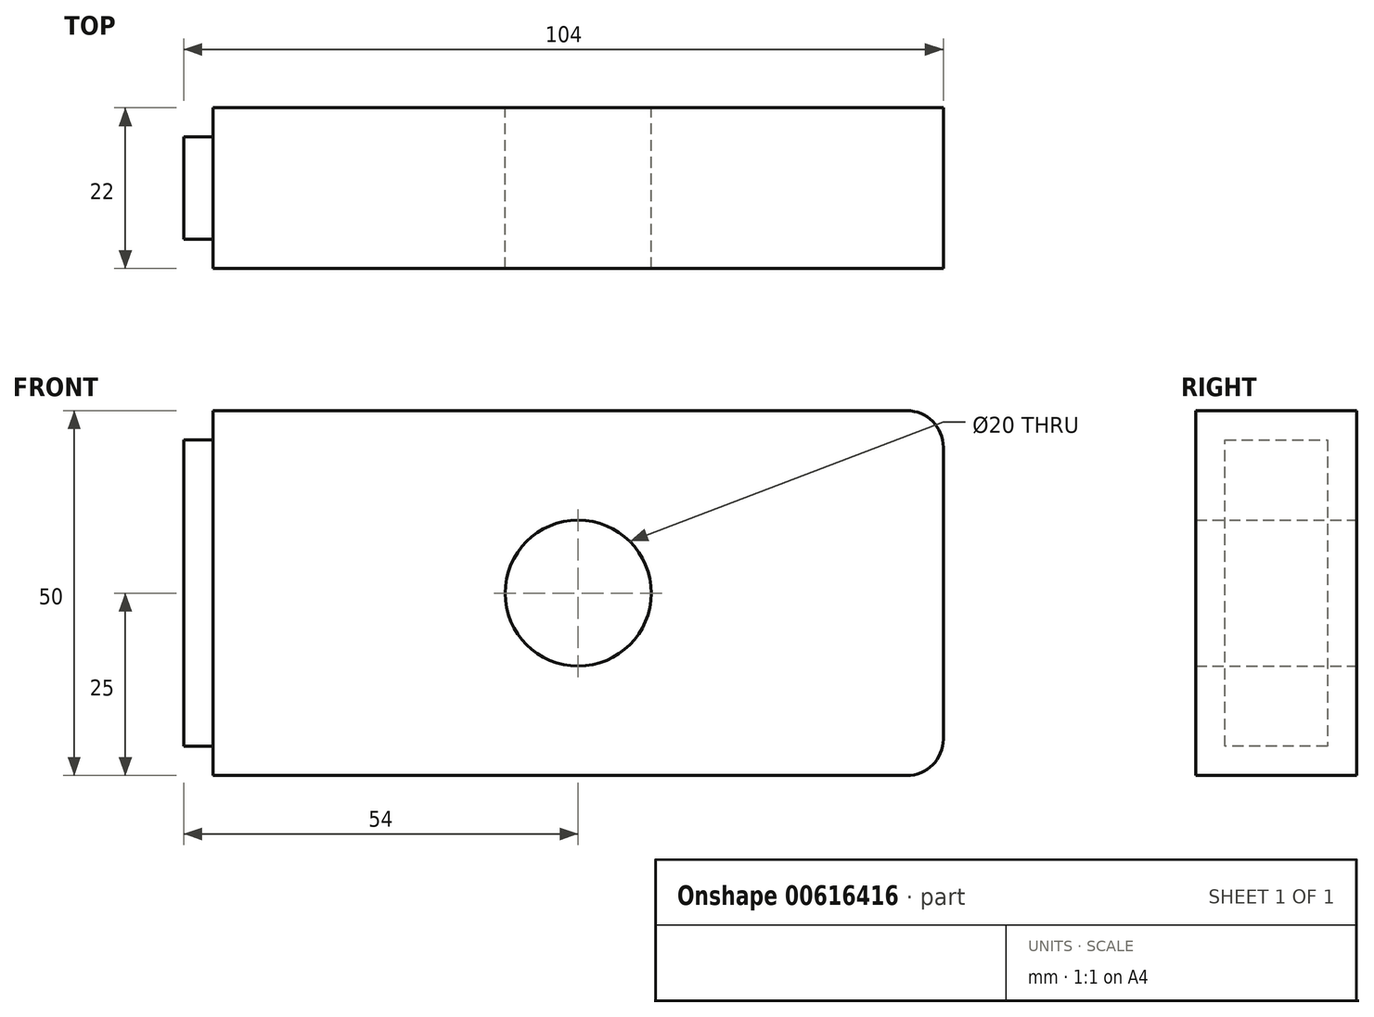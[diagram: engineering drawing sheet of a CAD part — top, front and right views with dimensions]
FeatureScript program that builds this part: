
annotation { "Feature Type Name" : "Feature", "Feature Type Description" : "" }
export const myFeature = defineFeature(function(context is Context, id is Id, definition is map)
    precondition{}
    {
        {
            var Q0;
            Q0=qCreatedBy(makeId("Front.planeOp"),FACE);
            var sketch = newSketch(context, id + "F0", { "sketchPlane" : qUnion([Q0])});
            skLineSegment(sketch, "E0.bottom", {"start": v(-50, 25) * mm, "end": v(45, 25) * mm});
            skLineSegment(sketch, "E0.top", {"start": v(-50, -25) * mm, "end": v(45, -25) * mm});
            skLineSegment(sketch, "E0.left", {"start": v(-50, 25) * mm, "end": v(-50, -25) * mm});
            skLineSegment(sketch, "E0.right", {"start": v(50, 20) * mm, "end": v(50, -20) * mm});
            skCircle(sketch, "E1", {"center": v(0, 0) * mm, "radius": 10 * mm});
            skLineSegment(sketch, "E2", {"start": v(-50, 0) * mm, "end": v(50, 0) * mm, "construction": true});
            skPoint(sketch, "E3.visualSharp", {"position": v(50, 25) * mm});
            skArc(sketch, "E3.filletArc", {"start": v(50, 20) * mm, "mid": v(48.54, 23.54) * mm, "end": v(45, 25) * mm});
            skPoint(sketch, "E4.visualSharp", {"position": v(50, -25) * mm});
            skArc(sketch, "E4.filletArc", {"start": v(45, -25) * mm, "mid": v(48.54, -23.54) * mm, "end": v(50, -20) * mm});
            skSolve(sketch);
        }
        {
            var Q0;
            Q0 = qSketchRegion(id + "F0", true);
            extrude(context, id + "F1", {"entities" : qUnion([Q0]), "depth" : 20 * mm, "offsetDistance" : 25 * mm});
        }
        {
            var Q0;
            Q0 = qSketchRegion(id + "F0", true);
            var Q1;
            Q1=makeQuery(id+"F1.opExtrude","CAP_FACE",FACE,{"disambiguationData":[OSD([sQuery(id+"F0.wireOp",EDGE,"E0.bottom"),sQuery(id+"F0.wireOp",EDGE,"E0.top"),sQuery(id+"F0.wireOp",EDGE,"E0.left"),sQuery(id+"F0.wireOp",EDGE,"E0.right"),sQuery(id+"F0.wireOp",EDGE,"E1")])],"isStart":false});
            extrude(context, id + "F2", {"entities" : qUnion([Q0, Q1]), "operationType" : NewBodyOperationType.ADD, "depth" : 2 * mm, "offsetDistance" : 25 * mm});
        }
        {
            var Q0;
            {var subQ0=sQuery(id+"F0.wireOp",EDGE,"E0.left");Q0=makeQuery(id+"F2.boolean.opBoolean","MERGE",FACE,{"derivedFrom":[makeQuery(id+"F1.opExtrude","SWEPT_FACE",FACE,{"disambiguationData":[OSD([subQ0])]}),makeQuery(id+"F2.opExtrude","SWEPT_FACE",FACE,{"disambiguationData":[OSD([subQ0]),TDD([makeQuery(id+"F1.opExtrude","CAP_EDGE",EDGE,{"disambiguationData":[OSD([subQ0])],"isStart":false})])]})]});}
            var sketch = newSketch(context, id + "F3", { "sketchPlane" : qUnion([Q0])});
            skLineSegment(sketch, "E5.0", {"start": v(18, 21) * mm, "end": v(4, 21) * mm});
            skLineSegment(sketch, "E5.1", {"start": v(18, -21) * mm, "end": v(18, 21) * mm});
            skLineSegment(sketch, "E5.2", {"start": v(4, -21) * mm, "end": v(18, -21) * mm});
            skLineSegment(sketch, "E5.3", {"start": v(4, 21) * mm, "end": v(4, -21) * mm});
            skSolve(sketch);
        }
        {
            var Q0;
            Q0=makeQuery(id+"F3.imprint","IMPRINT",FACE,{"disambiguationData":[TD([[makeQuery(id+"F3.imprint","IMPRINT",EDGE,{"derivedFrom":sQuery(id+"F3.wireOp",EDGE,"E5.0")}),1.0]])]});
            extrude(context, id + "F4", {"entities" : qUnion([Q0]), "operationType" : NewBodyOperationType.ADD, "depth" : 4 * mm, "offsetDistance" : 25 * mm});
        }
        {
            var Q0;
            {var subQ0=sQuery(id+"F0.wireOp",EDGE,"E0.right");Q0=makeQuery(id+"F2.boolean.opBoolean","MERGE",FACE,{"derivedFrom":[makeQuery(id+"F1.opExtrude","SWEPT_FACE",FACE,{"disambiguationData":[OSD([subQ0])]}),makeQuery(id+"F2.opExtrude","SWEPT_FACE",FACE,{"disambiguationData":[OSD([subQ0]),TDD([makeQuery(id+"F1.opExtrude","CAP_EDGE",EDGE,{"disambiguationData":[OSD([subQ0])],"isStart":false})])]})]});}
            var sketch = newSketch(context, id + "F5", { "sketchPlane" : qUnion([Q0])});
            skLineSegment(sketch, "E6", {"start": v(-22, 0) * mm, "end": v(0, 0) * mm});
            skSolve(sketch);
        }
        {
            var Q0;
            Q0=sQuery(id+"F5.wireOp",EDGE,"E6");
            extrude(context, id + "F6", {"bodyType" : ToolBodyType.SURFACE, "surfaceEntities" : qUnion([Q0]), "depth" : 30 * mm, "offsetDistance" : 25 * mm});
        }
    });
